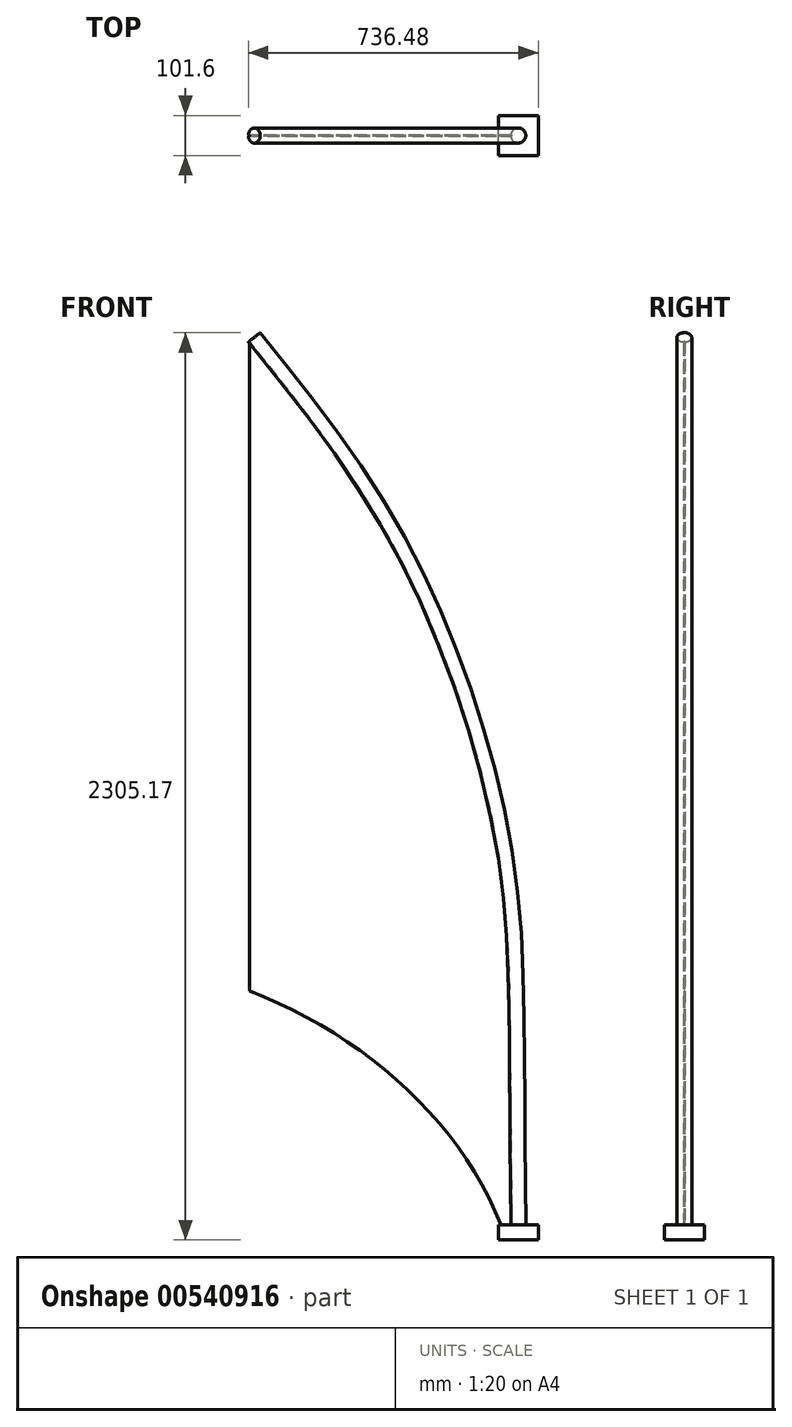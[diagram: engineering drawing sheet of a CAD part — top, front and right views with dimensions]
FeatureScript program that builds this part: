
annotation { "Feature Type Name" : "Feature", "Feature Type Description" : "" }
export const myFeature = defineFeature(function(context is Context, id is Id, definition is map)
    precondition{}
    {
        {
            var Q0;
            Q0=qCreatedBy(makeId("Front.planeOp"),FACE);
            var sketch = newSketch(context, id + "F0", { "sketchPlane" : qUnion([Q0])});
            skPoint(sketch, "E0", {"position": v(0, 0) * mm});
            skPoint(sketch, "E1", {"position": v(638.78, -594.32) * mm});
            skPoint(sketch, "E2", {"position": v(667.35, -594.32) * mm});
            skPoint(sketch, "E3", {"position": v(0, 1651) * mm});
            skLineSegment(sketch, "E4", {"start": v(0, 1651) * mm, "end": v(0, 0) * mm});
            skLineSegment(sketch, "E5", {"start": v(638.78, -594.32) * mm, "end": v(667.35, -594.32) * mm});
            skFitSpline(sketch, "E6", {"points": [v(0, 0) * mm, v(638.78, -594.32) * mm], "startDerivative": vector(858.83, -329.74) * mm, "endDerivative": vector(310.99, -801.16) * mm});
            skFitSpline(sketch, "E7", {"points": [v(0, 1651) * mm, v(401.4, 1064.84) * mm, v(628.66, 378.12) * mm, v(663.24, -120.85) * mm, v(667.35, -594.32) * mm], "startDerivative": vector(1946.18, -2409.83) * mm, "endDerivative": vector(18.73, -2581.85) * mm});
            skSolve(sketch);
        }
        {
            var Q0;
            Q0 = qSketchRegion(id + "F0", true);
            extrude(context, id + "F1", {"entities" : qUnion([Q0]), "depth" : 2.54 * mm, "offsetDistance" : 25.4 * mm});
        }
        {
            var Q0;
            Q0=makeQuery(id+"F1.opExtrude","SWEPT_FACE",FACE,{"disambiguationData":[OSD([sQuery(id+"F0.wireOp",EDGE,"E5")])]});
            var sketch = newSketch(context, id + "F2", { "sketchPlane" : qUnion([Q0])});
            skLineSegment(sketch, "E8", {"start": v(667.35, 1.27) * mm, "end": v(683.23, 1.27) * mm, "construction": true});
            skPoint(sketch, "E8.endSnap0", {"position": v(667.35, 1.27) * mm});
            skCircle(sketch, "E9", {"center": v(683.23, 1.27) * mm, "radius": 19.05 * mm});
            skSolve(sketch);
        }
        {
            var Q0;
            {var subQ1=sQuery(id+"F0.wireOp",EDGE,"E5");var subQ6=makeQuery(id+"F1.opExtrude","SWEPT_EDGE",EDGE,{"disambiguationData":[OSD([subQ1,sQuery(id+"F0.wireOp",EDGE,"E7")])]});Q0=makeQuery(id+"F2.imprint","IMPRINT",FACE,{"disambiguationData":[TD([[makeQuery(id+"F2.imprint","IMPRINT",EDGE,{"derivedFrom":subQ6}),1.0]])]});}
            var Q1;
            Q1=makeQuery(id+"F1.opExtrude","CAP_EDGE",EDGE,{"disambiguationData":[OSD([sQuery(id+"F0.wireOp",EDGE,"E7")])],"isStart":true});
            sweep(context, id + "F3", {"profiles" : qUnion([Q0]), "path" : qUnion([Q1])});
        }
        {
            var Q0;
            Q0=makeQuery(id+"F3.opSweep","CAP_FACE",FACE,{"disambiguationData":[OSD([sQuery(id+"F0.wireOp",EDGE,"E5"),sQuery(id+"F0.wireOp",EDGE,"E7"),sQuery(id+"F2.wireOp",EDGE,"E9")])],"isStart":true});
            var sketch = newSketch(context, id + "F4", { "sketchPlane" : qUnion([Q0])});
            skLineSegment(sketch, "E10.bottom", {"start": v(632.43, 52.07) * mm, "end": v(734.03, 52.07) * mm});
            skLineSegment(sketch, "E10.top", {"start": v(632.43, -49.53) * mm, "end": v(734.03, -49.53) * mm});
            skLineSegment(sketch, "E10.left", {"start": v(632.43, 52.07) * mm, "end": v(632.43, -49.53) * mm});
            skLineSegment(sketch, "E10.right", {"start": v(734.03, 52.07) * mm, "end": v(734.03, -49.53) * mm});
            skPoint(sketch, "E10.middle", {"position": v(683.23, 1.27) * mm});
            skSolve(sketch);
        }
        {
            var Q0;
            Q0 = qSketchRegion(id + "F4", true);
            extrude(context, id + "F5", {"entities" : qUnion([Q0]), "depth" : 38.1 * mm, "offsetDistance" : 25.4 * mm});
        }
    });
